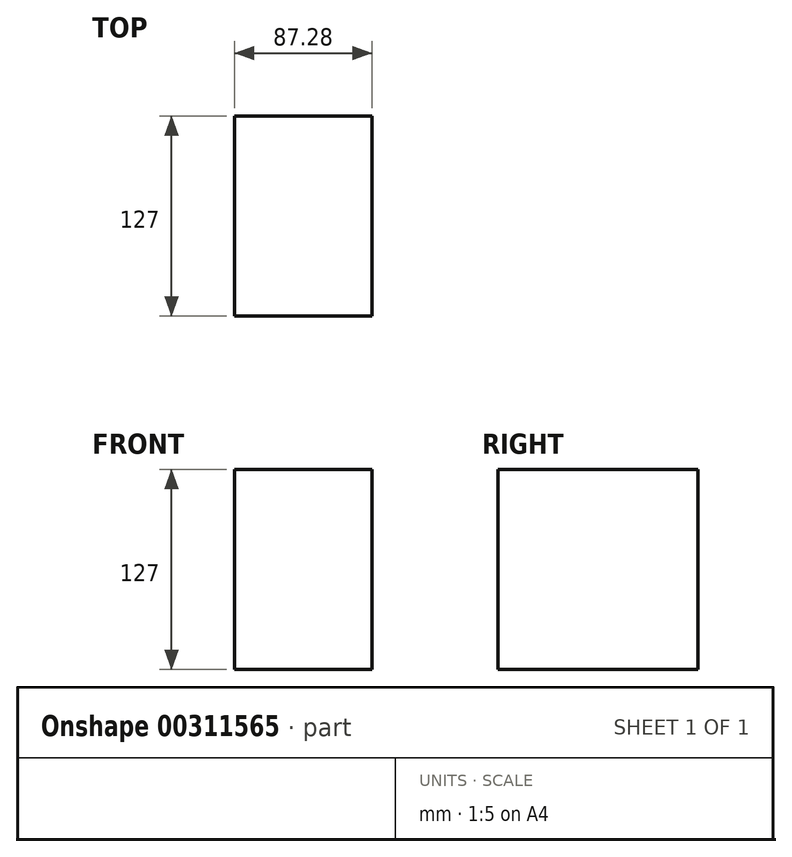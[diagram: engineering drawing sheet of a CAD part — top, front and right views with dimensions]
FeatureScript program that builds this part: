
annotation { "Feature Type Name" : "Feature", "Feature Type Description" : "" }
export const myFeature = defineFeature(function(context is Context, id is Id, definition is map)
    precondition{}
    {
        {
            var Q0;
            Q0=qCreatedBy(makeId("Front.planeOp"),FACE);
            var sketch = newSketch(context, id + "F0", { "sketchPlane" : qUnion([Q0])});
            skLineSegment(sketch, "E0.bottom", {"start": v(43.64, -63.5) * mm, "end": v(-43.64, -63.5) * mm});
            skLineSegment(sketch, "E0.top", {"start": v(43.64, 63.5) * mm, "end": v(-43.64, 63.5) * mm});
            skLineSegment(sketch, "E0.left", {"start": v(43.64, -63.5) * mm, "end": v(43.64, 63.5) * mm});
            skLineSegment(sketch, "E0.right", {"start": v(-43.64, -63.5) * mm, "end": v(-43.64, 63.5) * mm});
            skPoint(sketch, "E0.middle", {"position": v(0, 0) * mm});
            skSolve(sketch);
        }
        {
            var Q0;
            Q0=makeQuery(id+"F0.imprint","IMPRINT",FACE,{"disambiguationData":[TD([[makeQuery(id+"F0.imprint","IMPRINT",EDGE,{"derivedFrom":sQuery(id+"F0.wireOp",EDGE,"E0.bottom")}),-1.0]])]});
            extrude(context, id + "F1", {"entities" : qUnion([Q0]), "oppositeDirection" : true, "depth" : 127 * mm});
        }
    });
